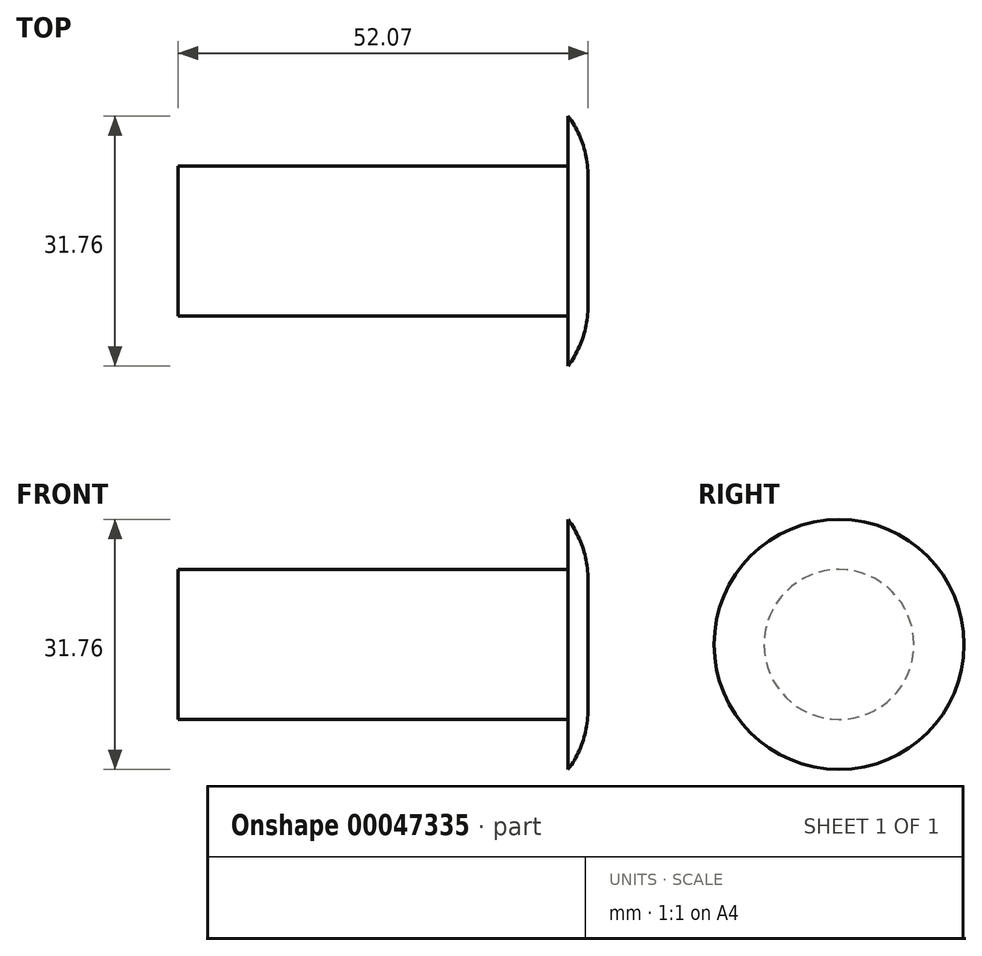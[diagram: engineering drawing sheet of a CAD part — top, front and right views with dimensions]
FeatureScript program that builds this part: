
annotation { "Feature Type Name" : "Feature", "Feature Type Description" : "" }
export const myFeature = defineFeature(function(context is Context, id is Id, definition is map)
    precondition{}
    {
        {
            var Q0;
            Q0=qCreatedBy(makeId("Right.planeOp"),FACE);
            var sketch = newSketch(context, id + "F0", { "sketchPlane" : qUnion([Q0])});
            skCircle(sketch, "E0", {"center": v(0, 0) * mm, "radius": 9.53 * mm});
            skSolve(sketch);
        }
        {
            var Q0;
            Q0=makeQuery(id+"F0.imprint","IMPRINT",FACE,{"disambiguationData":[TD([[makeQuery(id+"F0.imprint","IMPRINT",EDGE,{"derivedFrom":sQuery(id+"F0.wireOp",EDGE,"E0")}),1.0]])]});
            extrude(context, id + "F1", {"entities" : qUnion([Q0]), "depth" : 49.53 * mm});
        }
        {
            var Q0;
            Q0=makeQuery(id+"F1.opExtrude","CAP_FACE",FACE,{"disambiguationData":[OSD([sQuery(id+"F0.wireOp",EDGE,"E0")])],"isStart":false});
            var sketch = newSketch(context, id + "F2", { "sketchPlane" : qUnion([Q0])});
            skCircle(sketch, "E1", {"center": v(0, 0) * mm, "radius": 15.88 * mm});
            skSolve(sketch);
        }
        {
            var Q0;
            Q0=makeQuery(id+"F2.imprint","IMPRINT",FACE,{"disambiguationData":[TD([[makeQuery(id+"F2.imprint","IMPRINT",EDGE,{"derivedFrom":sQuery(id+"F2.wireOp",EDGE,"E1")}),1.0]])]});
            var Q1;
            Q1=makeQuery(id+"F2.imprint","IMPRINT",FACE,{"disambiguationData":[TD([[makeQuery(id+"F2.imprint","IMPRINT",EDGE,{"derivedFrom":makeQuery(id+"F1.opExtrude","CAP_EDGE",EDGE,{"disambiguationData":[OSD([sQuery(id+"F0.wireOp",EDGE,"E0")])],"isStart":false})}),1.0]])]});
            extrude(context, id + "F3", {"entities" : qUnion([Q0, Q1]), "operationType" : NewBodyOperationType.ADD, "depth" : 2.54 * mm});
        }
        {
            var Q0;
            Q0=makeQuery(id+"F3.opExtrude","CAP_FACE",FACE,{"disambiguationData":[OSD([sQuery(id+"F2.wireOp",EDGE,"E1")])],"isStart":false});
            fillet(context, id + "F4", {"entities" : qUnion([Q0]), "radius" : 12.7 * mm, "tangentPropagation" : true, "allowEdgeOverflow" : false});
        }
    });
